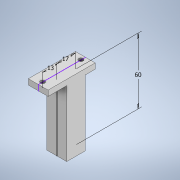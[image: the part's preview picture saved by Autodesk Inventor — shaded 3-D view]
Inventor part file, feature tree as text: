
AUTODESK INVENTOR PART (.ipt)
format: ipt  version: 2020.3 (Build 243373000, 373)  size: 112,128 bytes
history: native  units: mm
features: extrude x2, sketch x2
ambient origin geometry x8: Origin, YZ Plane, XZ Plane, XY Plane, X Axis, Y Axis, Z Axis, Center Point
bodies: Solid1 (feature_tree)
feature tree (4):
  extrude  "Extrusion1"  Depth=60.0mm
  extrude  "Extrusion2"  Depth=18.0mm TaperAngle=0.0deg
  sketch  "Sketch1"  dims[d0=17.0mm d1=60.0mm]
  sketch  "Sketch2"  dims[d2=13.0mm d3=18.0mm d4=0.0mm d5=4.0mm d6=4.0mm d7=10.0mm d8=0.0mm]
